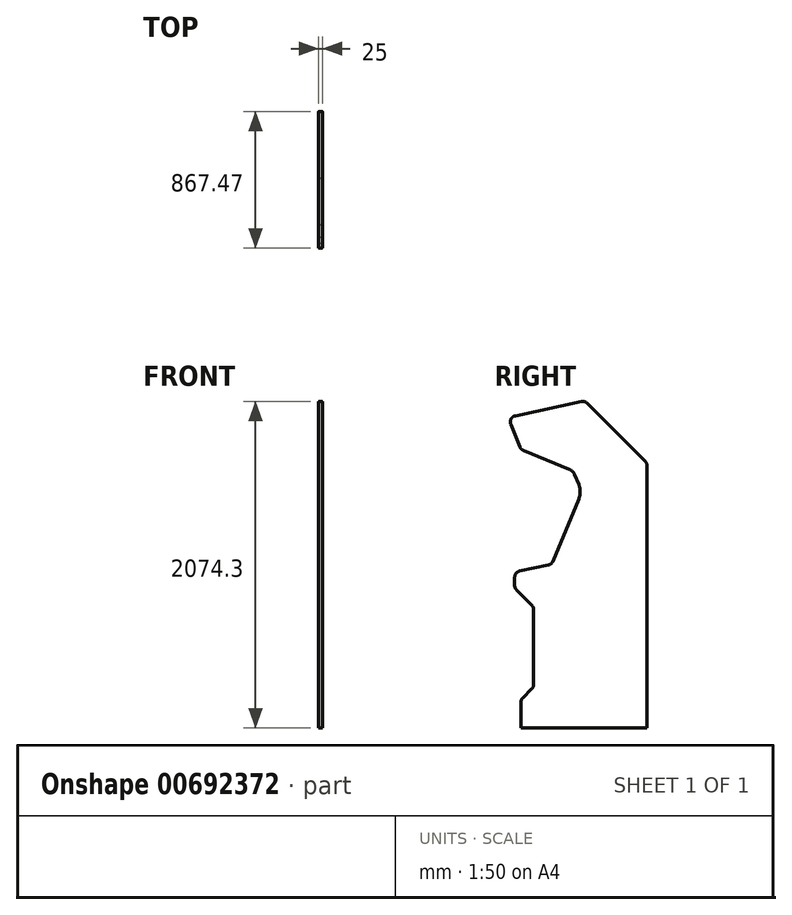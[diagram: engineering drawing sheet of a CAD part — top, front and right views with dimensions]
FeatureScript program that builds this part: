
annotation { "Feature Type Name" : "Feature", "Feature Type Description" : "" }
export const myFeature = defineFeature(function(context is Context, id is Id, definition is map)
    precondition{}
    {
        {
            var Q0;
            Q0=qCreatedBy(makeId("Right.planeOp"),FACE);
            var sketch = newSketch(context, id + "F0", { "sketchPlane" : qUnion([Q0])});
            skLineSegment(sketch, "E0", {"start": v(0, 0) * mm, "end": v(800, 0) * mm});
            skLineSegment(sketch, "E1", {"start": v(0, 0) * mm, "end": v(0, 180) * mm});
            skLineSegment(sketch, "E2", {"start": v(0, 180) * mm, "end": v(80, 260) * mm});
            skLineSegment(sketch, "E3", {"start": v(80, 260) * mm, "end": v(80, 770) * mm});
            skLineSegment(sketch, "E4", {"start": v(80, 770) * mm, "end": v(-40, 890) * mm});
            skLineSegment(sketch, "E5", {"start": v(-40, 890) * mm, "end": v(-40, 990) * mm});
            skLineSegment(sketch, "E6", {"start": v(-40, 990) * mm, "end": v(194.76, 1039.9) * mm});
            skLineSegment(sketch, "E7", {"start": v(194.76, 1039.9) * mm, "end": v(424.37, 1594.23) * mm});
            skLineSegment(sketch, "E8", {"start": v(424.37, 1594.23) * mm, "end": v(0, 1770) * mm});
            skLineSegment(sketch, "E9", {"start": v(0, 1770) * mm, "end": v(-82.41, 1973.98) * mm});
            skLineSegment(sketch, "E10", {"start": v(-82.41, 1973.98) * mm, "end": v(406.66, 2077.94) * mm});
            skLineSegment(sketch, "E11", {"start": v(406.66, 2077.94) * mm, "end": v(800, 1684.6) * mm});
            skLineSegment(sketch, "E12", {"start": v(800, 1684.6) * mm, "end": v(800, 0) * mm});
            skSolve(sketch);
        }
        {
            var Q0;
            Q0=makeQuery(id+"F0.imprint","IMPRINT",FACE,{"disambiguationData":[TD([[makeQuery(id+"F0.imprint","IMPRINT",EDGE,{"derivedFrom":sQuery(id+"F0.wireOp",EDGE,"E0")}),1.0]])]});
            extrude(context, id + "F1", {"entities" : qUnion([Q0]), "depth" : 25 * mm, "offsetDistance" : 25 * mm});
        }
        {
            var Q0;
            Q0=makeQuery(id+"F1.opExtrude","SWEPT_EDGE",EDGE,{"disambiguationData":[OSD([sQuery(id+"F0.wireOp",EDGE,"E6"),sQuery(id+"F0.wireOp",EDGE,"E7")])]});
            var Q1;
            Q1=makeQuery(id+"F1.opExtrude","SWEPT_EDGE",EDGE,{"disambiguationData":[OSD([sQuery(id+"F0.wireOp",EDGE,"E8"),sQuery(id+"F0.wireOp",EDGE,"E9")])]});
            var Q2;
            Q2=makeQuery(id+"F1.opExtrude","SWEPT_EDGE",EDGE,{"disambiguationData":[OSD([sQuery(id+"F0.wireOp",EDGE,"E9"),sQuery(id+"F0.wireOp",EDGE,"E10")])]});
            var Q3;
            Q3=makeQuery(id+"F1.opExtrude","SWEPT_EDGE",EDGE,{"disambiguationData":[OSD([sQuery(id+"F0.wireOp",EDGE,"E10"),sQuery(id+"F0.wireOp",EDGE,"E11")])]});
            var Q4;
            Q4=makeQuery(id+"F1.opExtrude","SWEPT_EDGE",EDGE,{"disambiguationData":[OSD([sQuery(id+"F0.wireOp",EDGE,"E11"),sQuery(id+"F0.wireOp",EDGE,"E12")])]});
            var Q5;
            Q5=makeQuery(id+"F1.opExtrude","SWEPT_EDGE",EDGE,{"disambiguationData":[OSD([sQuery(id+"F0.wireOp",EDGE,"E5"),sQuery(id+"F0.wireOp",EDGE,"E6")])]});
            var Q6;
            Q6=makeQuery(id+"F1.opExtrude","SWEPT_EDGE",EDGE,{"disambiguationData":[OSD([sQuery(id+"F0.wireOp",EDGE,"E4"),sQuery(id+"F0.wireOp",EDGE,"E5")])]});
            var Q7;
            Q7=makeQuery(id+"F1.opExtrude","SWEPT_EDGE",EDGE,{"disambiguationData":[OSD([sQuery(id+"F0.wireOp",EDGE,"E3"),sQuery(id+"F0.wireOp",EDGE,"E4")])]});
            var Q8;
            Q8=makeQuery(id+"F1.opExtrude","SWEPT_EDGE",EDGE,{"disambiguationData":[OSD([sQuery(id+"F0.wireOp",EDGE,"E2"),sQuery(id+"F0.wireOp",EDGE,"E3")])]});
            var Q9;
            Q9=makeQuery(id+"F1.opExtrude","SWEPT_EDGE",EDGE,{"disambiguationData":[OSD([sQuery(id+"F0.wireOp",EDGE,"E1"),sQuery(id+"F0.wireOp",EDGE,"E2")])]});
            fillet(context, id + "F2", {"entities" : qUnion([Q0, Q1, Q2, Q3, Q4, Q5, Q6, Q7, Q8, Q9]), "radius" : 40 * mm, "tangentPropagation" : true, "allowEdgeOverflow" : false});
        }
        {
            var Q0;
            Q0=makeQuery(id+"F1.opExtrude","SWEPT_EDGE",EDGE,{"disambiguationData":[OSD([sQuery(id+"F0.wireOp",EDGE,"E7"),sQuery(id+"F0.wireOp",EDGE,"E8")])]});
            chamfer(context, id + "F3", {"entities" : qUnion([Q0]), "width" : 100 * mm, "tangentPropagation" : true});
        }
        {
            var Q0;
            {var subQ0=sQuery(id+"F0.wireOp",EDGE,"E7");Q0=makeQuery(id+"F3.opChamfer","BLEND_EDGE",EDGE,{"blendedFrom":[makeQuery(id+"F1.opExtrude","SWEPT_EDGE",EDGE,{"disambiguationData":[OSD([subQ0,sQuery(id+"F0.wireOp",EDGE,"E8")])]}),makeQuery(id+"F1.opExtrude","SWEPT_FACE",FACE,{"disambiguationData":[OSD([subQ0])]})],"blendedInto":[makeQuery(id+"F1.opExtrude","SWEPT_FACE",FACE,{"disambiguationData":[OSD([subQ0])]})]});}
            fillet(context, id + "F4", {"entities" : qUnion([Q0]), "radius" : 120 * mm, "tangentPropagation" : true, "allowEdgeOverflow" : false});
        }
        {
            var Q0;
            {var subQ0=sQuery(id+"F0.wireOp",EDGE,"E8");Q0=makeQuery(id+"F3.opChamfer","BLEND_EDGE",EDGE,{"blendedFrom":[makeQuery(id+"F1.opExtrude","SWEPT_EDGE",EDGE,{"disambiguationData":[OSD([sQuery(id+"F0.wireOp",EDGE,"E7"),subQ0])]}),makeQuery(id+"F1.opExtrude","SWEPT_FACE",FACE,{"disambiguationData":[OSD([subQ0])]})],"blendedInto":[makeQuery(id+"F1.opExtrude","SWEPT_FACE",FACE,{"disambiguationData":[OSD([subQ0])]})]});}
            fillet(context, id + "F5", {"entities" : qUnion([Q0]), "radius" : 60 * mm, "tangentPropagation" : true, "allowEdgeOverflow" : false});
        }
    });
